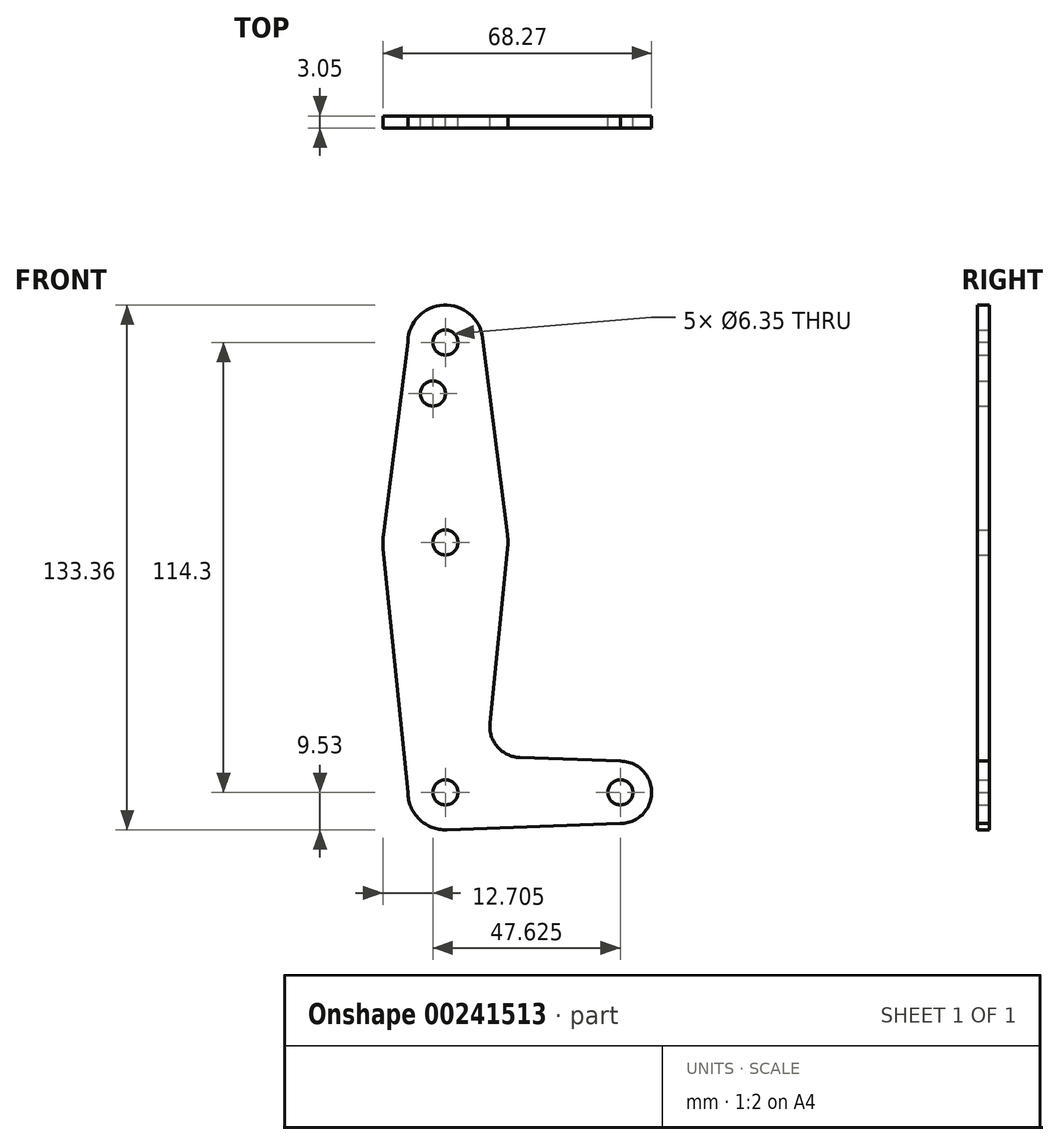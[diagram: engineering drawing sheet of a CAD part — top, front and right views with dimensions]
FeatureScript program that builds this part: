
annotation { "Feature Type Name" : "Feature", "Feature Type Description" : "" }
export const myFeature = defineFeature(function(context is Context, id is Id, definition is map)
    precondition{}
    {
        {
            var Q0;
            Q0=qCreatedBy(makeId("Front.planeOp"),FACE);
            var sketch = newSketch(context, id + "F0", { "sketchPlane" : qUnion([Q0])});
            skLineSegment(sketch, "E0", {"start": v(0, 0) * mm, "end": v(44.45, 0) * mm});
            skLineSegment(sketch, "E1", {"start": v(0, 0) * mm, "end": v(0, 63.5) * mm});
            skLineSegment(sketch, "E2", {"start": v(0, 63.5) * mm, "end": v(0, 114.3) * mm});
            skCircle(sketch, "E3", {"center": v(0, 114.3) * mm, "radius": 9.53 * mm});
            skCircle(sketch, "E4", {"center": v(0, 63.5) * mm, "radius": 15.88 * mm});
            skCircle(sketch, "E5", {"center": v(0, 0) * mm, "radius": 9.53 * mm});
            skCircle(sketch, "E6", {"center": v(44.45, 0) * mm, "radius": 7.94 * mm});
            skLineSegment(sketch, "E7", {"start": v(44.45, 7.94) * mm, "end": v(18.93, 8.85) * mm});
            skLineSegment(sketch, "E8", {"start": v(44.36, -7.94) * mm, "end": v(0, -9.53) * mm});
            skLineSegment(sketch, "E9", {"start": v(11.3, 17.6) * mm, "end": v(15.8, 61.9) * mm});
            skLineSegment(sketch, "E10", {"start": v(-9.52, 0) * mm, "end": v(-15.8, 61.9) * mm});
            skLineSegment(sketch, "E11", {"start": v(-9.52, 114.47) * mm, "end": v(-15.75, 65.5) * mm});
            skLineSegment(sketch, "E12", {"start": v(9.46, 115.4) * mm, "end": v(15.75, 65.48) * mm});
            skCircle(sketch, "E13", {"center": v(0, 114.3) * mm, "radius": 3.18 * mm});
            skCircle(sketch, "E14", {"center": v(0, 63.5) * mm, "radius": 3.18 * mm});
            skCircle(sketch, "E15", {"center": v(0, 0) * mm, "radius": 3.18 * mm});
            skCircle(sketch, "E16", {"center": v(44.45, 0) * mm, "radius": 3.18 * mm});
            skArc(sketch, "E17.filletArc", {"start": v(11.3, 17.6) * mm, "mid": v(13.22, 11.57) * mm, "end": v(18.93, 8.85) * mm});
            skCircle(sketch, "E18", {"center": v(-3.18, 101.35) * mm, "radius": 3.18 * mm});
            skSolve(sketch);
        }
        {
            var Q0;
            Q0 = qSketchRegion(id + "F0", true);
            var Q1;
            {var subQ0=sQuery(id+"F0.wireOp",EDGE,"E15");var subQ1=sQuery(id+"F0.wireOp",EDGE,"E0");var subQ2=makeQuery(id+"F0.imprint","INTERSECT",VERTEX,{"derivedFrom":[subQ1,subQ0]});Q1=makeQuery(id+"F0.imprint","IMPRINT",FACE,{"disambiguationData":[TD([[makeQuery(id+"F0.imprint","IMPRINT",EDGE,{"disambiguationData":[TD([[subQ2,-1.0]])],"derivedFrom":subQ1}),1.0]])]});}
            extrude(context, id + "F1", {"entities" : qUnion([Q0, Q1]), "depth" : 3.05 * mm});
        }
    });
